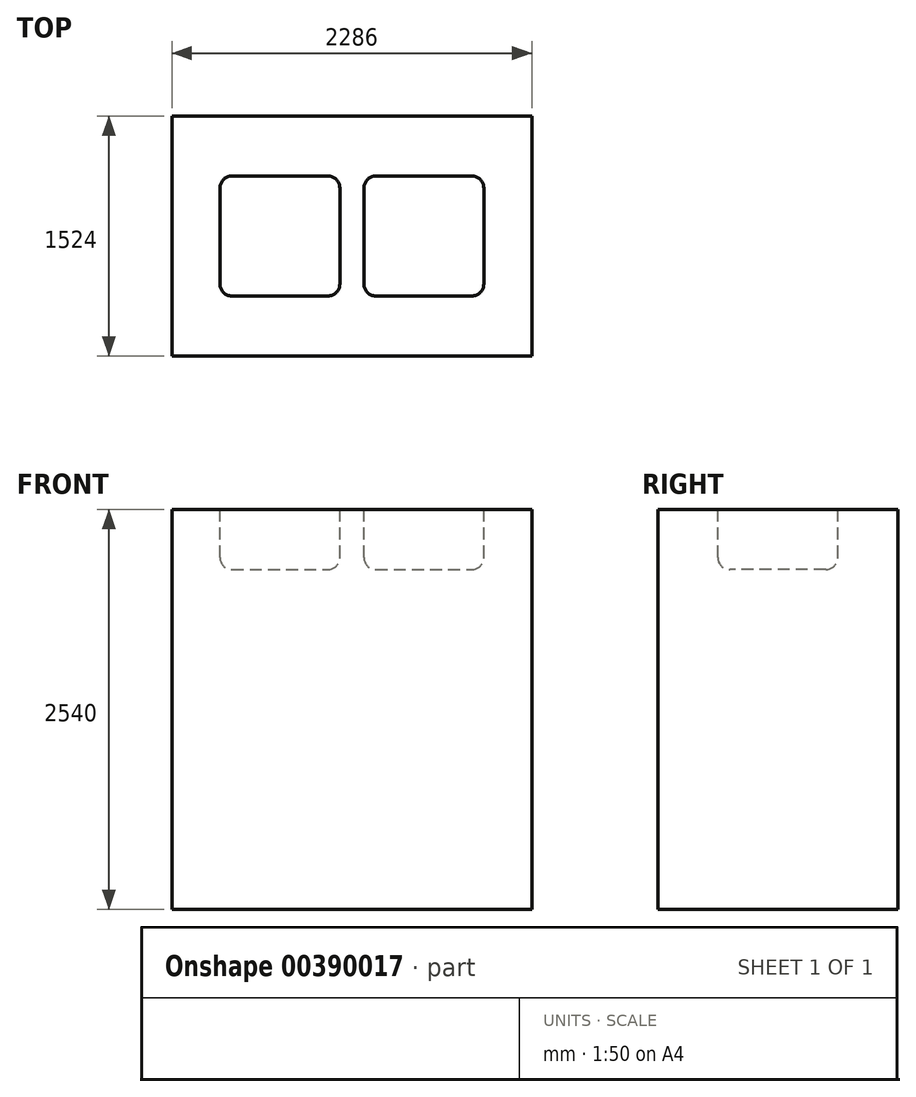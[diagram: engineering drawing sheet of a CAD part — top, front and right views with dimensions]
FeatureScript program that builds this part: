
annotation { "Feature Type Name" : "Feature", "Feature Type Description" : "" }
export const myFeature = defineFeature(function(context is Context, id is Id, definition is map)
    precondition{}
    {
        {
            var Q0;
            Q0=qCreatedBy(makeId("Top.planeOp"),FACE);
            var sketch = newSketch(context, id + "F0", { "sketchPlane" : qUnion([Q0])});
            skLineSegment(sketch, "E0.bottom", {"start": v(1143, 762) * mm, "end": v(-1143, 762) * mm});
            skLineSegment(sketch, "E0.top", {"start": v(1143, -762) * mm, "end": v(-1143, -762) * mm});
            skLineSegment(sketch, "E0.left", {"start": v(1143, 762) * mm, "end": v(1143, -762) * mm});
            skLineSegment(sketch, "E0.right", {"start": v(-1143, 762) * mm, "end": v(-1143, -762) * mm});
            skPoint(sketch, "E0.middle", {"position": v(0, 0) * mm});
            skSolve(sketch);
        }
        {
            var Q0;
            Q0 = qSketchRegion(id + "F0", true);
            extrude(context, id + "F1", {"entities" : qUnion([Q0]), "depth" : 2540 * mm});
        }
        {
            var Q0;
            Q0=makeQuery(id+"F1.opExtrude","CAP_FACE",FACE,{"disambiguationData":[OSD([sQuery(id+"F0.wireOp",EDGE,"E0.bottom"),sQuery(id+"F0.wireOp",EDGE,"E0.top"),sQuery(id+"F0.wireOp",EDGE,"E0.left"),sQuery(id+"F0.wireOp",EDGE,"E0.right")])],"isStart":false});
            var sketch = newSketch(context, id + "F2", { "sketchPlane" : qUnion([Q0])});
            skLineSegment(sketch, "E1.bottom", {"start": v(-838.2, 381) * mm, "end": v(-76.2, 381) * mm});
            skLineSegment(sketch, "E1.top", {"start": v(-838.2, -381) * mm, "end": v(-76.2, -381) * mm});
            skLineSegment(sketch, "E1.left", {"start": v(-838.2, 381) * mm, "end": v(-838.2, -381) * mm});
            skLineSegment(sketch, "E1.right", {"start": v(-76.2, 381) * mm, "end": v(-76.2, -381) * mm});
            skSolve(sketch);
        }
        {
            var Q0;
            Q0 = qSketchRegion(id + "F2", true);
            extrude(context, id + "F3", {"entities" : qUnion([Q0]), "operationType" : NewBodyOperationType.REMOVE, "oppositeDirection" : true, "depth" : 381 * mm});
        }
        {
            var Q0;
            Q0=makeQuery(id+"F3.boolean.opBoolean","COPY",EDGE,{"derivedFrom":makeQuery(id+"F3.opExtrude","SWEPT_EDGE",EDGE,{"disambiguationData":[OSD([sQuery(id+"F2.wireOp",EDGE,"E1.bottom"),sQuery(id+"F2.wireOp",EDGE,"E1.left")])]})});
            var Q1;
            Q1=makeQuery(id+"F3.boolean.opBoolean","COPY",EDGE,{"derivedFrom":makeQuery(id+"F3.opExtrude","CAP_EDGE",EDGE,{"disambiguationData":[OSD([sQuery(id+"F2.wireOp",EDGE,"E1.left")])],"isStart":false})});
            var Q2;
            Q2=makeQuery(id+"F3.boolean.opBoolean","COPY",EDGE,{"derivedFrom":makeQuery(id+"F3.opExtrude","CAP_EDGE",EDGE,{"disambiguationData":[OSD([sQuery(id+"F2.wireOp",EDGE,"E1.bottom")])],"isStart":false})});
            var Q3;
            Q3=makeQuery(id+"F3.boolean.opBoolean","COPY",EDGE,{"derivedFrom":makeQuery(id+"F3.opExtrude","CAP_EDGE",EDGE,{"disambiguationData":[OSD([sQuery(id+"F2.wireOp",EDGE,"E1.right")])],"isStart":false})});
            var Q4;
            Q4=makeQuery(id+"F3.boolean.opBoolean","COPY",EDGE,{"derivedFrom":makeQuery(id+"F3.opExtrude","SWEPT_EDGE",EDGE,{"disambiguationData":[OSD([sQuery(id+"F2.wireOp",EDGE,"E1.bottom"),sQuery(id+"F2.wireOp",EDGE,"E1.right")])]})});
            var Q5;
            Q5=makeQuery(id+"F3.boolean.opBoolean","COPY",EDGE,{"derivedFrom":makeQuery(id+"F3.opExtrude","CAP_EDGE",EDGE,{"disambiguationData":[OSD([sQuery(id+"F2.wireOp",EDGE,"E1.top")])],"isStart":false})});
            var Q6;
            Q6=makeQuery(id+"F3.boolean.opBoolean","COPY",EDGE,{"derivedFrom":makeQuery(id+"F3.opExtrude","SWEPT_EDGE",EDGE,{"disambiguationData":[OSD([sQuery(id+"F2.wireOp",EDGE,"E1.top"),sQuery(id+"F2.wireOp",EDGE,"E1.right")])]})});
            var Q7;
            Q7=makeQuery(id+"F3.boolean.opBoolean","COPY",EDGE,{"derivedFrom":makeQuery(id+"F3.opExtrude","SWEPT_EDGE",EDGE,{"disambiguationData":[OSD([sQuery(id+"F2.wireOp",EDGE,"E1.top"),sQuery(id+"F2.wireOp",EDGE,"E1.left")])]})});
            fillet(context, id + "F4", {"entities" : qUnion([Q0, Q1, Q2, Q3, Q4, Q5, Q6, Q7]), "radius" : 76.2 * mm, "tangentPropagation" : true, "allowEdgeOverflow" : false});
        }
        {
            var Q0;
            Q0=makeQuery(id+"F1.opExtrude","CAP_FACE",FACE,{"disambiguationData":[OSD([sQuery(id+"F0.wireOp",EDGE,"E0.bottom"),sQuery(id+"F0.wireOp",EDGE,"E0.top"),sQuery(id+"F0.wireOp",EDGE,"E0.left"),sQuery(id+"F0.wireOp",EDGE,"E0.right")])],"isStart":false});
            var sketch = newSketch(context, id + "F5", { "sketchPlane" : qUnion([Q0])});
            skLineSegment(sketch, "E2.bottom", {"start": v(76.2, 381) * mm, "end": v(838.2, 381) * mm});
            skLineSegment(sketch, "E2.top", {"start": v(76.2, -381) * mm, "end": v(838.2, -381) * mm});
            skLineSegment(sketch, "E2.left", {"start": v(76.2, 381) * mm, "end": v(76.2, -381) * mm});
            skLineSegment(sketch, "E2.right", {"start": v(838.2, 381) * mm, "end": v(838.2, -381) * mm});
            skSolve(sketch);
        }
        {
            var Q0;
            Q0 = qSketchRegion(id + "F5", true);
            extrude(context, id + "F6", {"entities" : qUnion([Q0]), "operationType" : NewBodyOperationType.REMOVE, "oppositeDirection" : true, "depth" : 381 * mm});
        }
        {
            var Q0;
            Q0=makeQuery(id+"F6.boolean.opBoolean","COPY",EDGE,{"derivedFrom":makeQuery(id+"F6.opExtrude","SWEPT_EDGE",EDGE,{"disambiguationData":[OSD([sQuery(id+"F5.wireOp",EDGE,"E2.bottom"),sQuery(id+"F5.wireOp",EDGE,"E2.left")])]})});
            var Q1;
            Q1=makeQuery(id+"F6.boolean.opBoolean","COPY",EDGE,{"derivedFrom":makeQuery(id+"F6.opExtrude","CAP_EDGE",EDGE,{"disambiguationData":[OSD([sQuery(id+"F5.wireOp",EDGE,"E2.bottom")])],"isStart":false})});
            var Q2;
            Q2=makeQuery(id+"F6.boolean.opBoolean","COPY",EDGE,{"derivedFrom":makeQuery(id+"F6.opExtrude","CAP_EDGE",EDGE,{"disambiguationData":[OSD([sQuery(id+"F5.wireOp",EDGE,"E2.left")])],"isStart":false})});
            var Q3;
            Q3=makeQuery(id+"F6.boolean.opBoolean","COPY",EDGE,{"derivedFrom":makeQuery(id+"F6.opExtrude","CAP_EDGE",EDGE,{"disambiguationData":[OSD([sQuery(id+"F5.wireOp",EDGE,"E2.right")])],"isStart":false})});
            var Q4;
            Q4=makeQuery(id+"F6.boolean.opBoolean","COPY",EDGE,{"derivedFrom":makeQuery(id+"F6.opExtrude","SWEPT_EDGE",EDGE,{"disambiguationData":[OSD([sQuery(id+"F5.wireOp",EDGE,"E2.bottom"),sQuery(id+"F5.wireOp",EDGE,"E2.right")])]})});
            var Q5;
            Q5=makeQuery(id+"F6.boolean.opBoolean","COPY",EDGE,{"derivedFrom":makeQuery(id+"F6.opExtrude","SWEPT_EDGE",EDGE,{"disambiguationData":[OSD([sQuery(id+"F5.wireOp",EDGE,"E2.top"),sQuery(id+"F5.wireOp",EDGE,"E2.right")])]})});
            var Q6;
            Q6=makeQuery(id+"F6.boolean.opBoolean","COPY",EDGE,{"derivedFrom":makeQuery(id+"F6.opExtrude","CAP_EDGE",EDGE,{"disambiguationData":[OSD([sQuery(id+"F5.wireOp",EDGE,"E2.top")])],"isStart":false})});
            var Q7;
            Q7=makeQuery(id+"F6.boolean.opBoolean","COPY",EDGE,{"derivedFrom":makeQuery(id+"F6.opExtrude","SWEPT_EDGE",EDGE,{"disambiguationData":[OSD([sQuery(id+"F5.wireOp",EDGE,"E2.top"),sQuery(id+"F5.wireOp",EDGE,"E2.left")])]})});
            fillet(context, id + "F7", {"entities" : qUnion([Q0, Q1, Q2, Q3, Q4, Q5, Q6, Q7]), "radius" : 76.2 * mm, "tangentPropagation" : true, "allowEdgeOverflow" : false});
        }
    });
